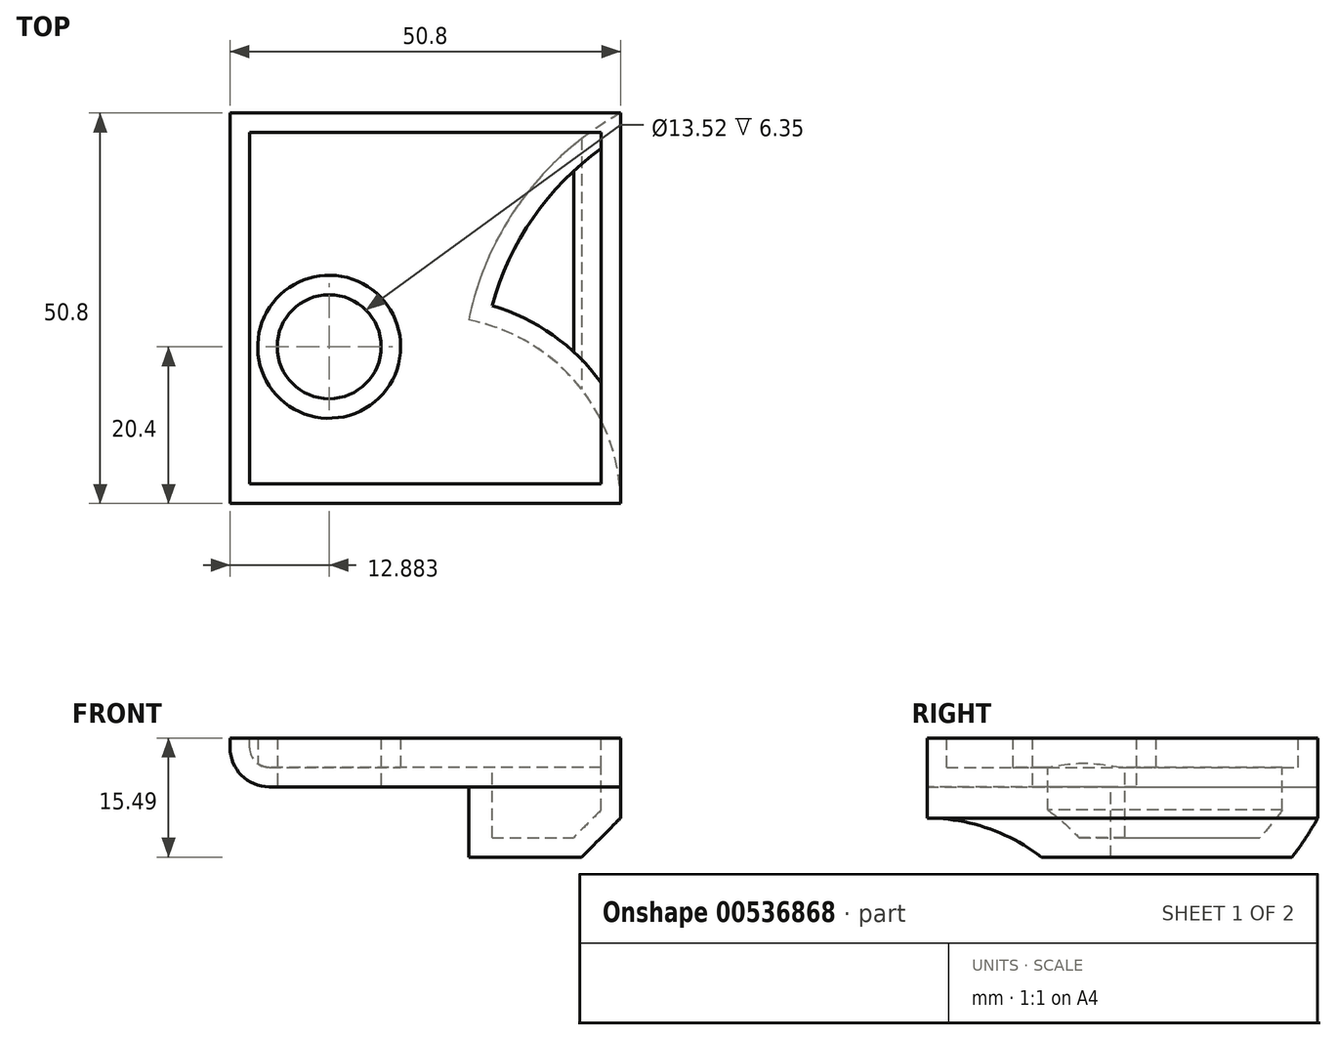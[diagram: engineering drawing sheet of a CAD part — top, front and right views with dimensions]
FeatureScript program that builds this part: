
annotation { "Feature Type Name" : "Feature", "Feature Type Description" : "" }
export const myFeature = defineFeature(function(context is Context, id is Id, definition is map)
    precondition{}
    {
        {
            var Q0;
            Q0=qCreatedBy(makeId("Top.planeOp"),FACE);
            var sketch = newSketch(context, id + "F0", { "sketchPlane" : qUnion([Q0])});
            skLineSegment(sketch, "E0.bottom", {"start": v(0, 0) * mm, "end": v(-50.8, 0) * mm});
            skLineSegment(sketch, "E0.top", {"start": v(0, 50.8) * mm, "end": v(-50.8, 50.8) * mm});
            skLineSegment(sketch, "E0.left", {"start": v(0, 0) * mm, "end": v(0, 50.8) * mm});
            skLineSegment(sketch, "E0.right", {"start": v(-50.8, 0) * mm, "end": v(-50.8, 50.8) * mm});
            skSolve(sketch);
        }
        {
            var Q0;
            Q0=makeQuery(id+"F0.imprint","IMPRINT",FACE,{"disambiguationData":[TD([[makeQuery(id+"F0.imprint","IMPRINT",EDGE,{"derivedFrom":sQuery(id+"F0.wireOp",EDGE,"E0.bottom")}),-1.0]])]});
            extrude(context, id + "F1", {"entities" : qUnion([Q0]), "oppositeDirection" : true, "depth" : 6.35 * mm, "offsetDistance" : 25.4 * mm});
        }
        {
            var Q0;
            Q0=makeQuery(id+"F1.opExtrude","CAP_FACE",FACE,{"disambiguationData":[OSD([sQuery(id+"F0.wireOp",EDGE,"E0.bottom"),sQuery(id+"F0.wireOp",EDGE,"E0.top"),sQuery(id+"F0.wireOp",EDGE,"E0.left"),sQuery(id+"F0.wireOp",EDGE,"E0.right")])],"isStart":false});
            var sketch = newSketch(context, id + "F2", { "sketchPlane" : qUnion([Q0])});
            skArc(sketch, "E1", {"start": v(-19.78, -23.88) * mm, "mid": v(-12.85, -39.52) * mm, "end": v(0, -50.8) * mm});
            skArc(sketch, "E2", {"start": v(-19.78, -23.88) * mm, "mid": v(-5.59, -15.5) * mm, "end": v(0, 0) * mm});
            skCircle(sketch, "E3", {"center": v(-37.92, -20.4) * mm, "radius": 6.76 * mm});
            skSolve(sketch);
        }
        {
            var Q0;
            Q0=makeQuery(id+"F2.imprint","IMPRINT",FACE,{"disambiguationData":[TD([[makeQuery(id+"F2.imprint","IMPRINT",EDGE,{"derivedFrom":sQuery(id+"F2.wireOp",EDGE,"E1")}),1.0]])]});
            extrude(context, id + "F3", {"entities" : qUnion([Q0]), "operationType" : NewBodyOperationType.ADD, "depth" : 9.14 * mm, "offsetDistance" : 25.4 * mm});
        }
        {
            var Q0;
            Q0 = qSketchRegion(id + "F2", true);
            extrude(context, id + "F4", {"entities" : qUnion([Q0]), "operationType" : NewBodyOperationType.REMOVE, "oppositeDirection" : true, "depth" : 25.4 * mm, "offsetDistance" : 25.4 * mm});
        }
        {
            var Q0;
            Q0=makeQuery(id+"F1.opExtrude","CAP_EDGE",EDGE,{"disambiguationData":[OSD([sQuery(id+"F0.wireOp",EDGE,"E0.right")])],"isStart":false});
            fillet(context, id + "F5", {"entities" : qUnion([Q0]), "radius" : 5.08 * mm, "tangentPropagation" : true, "allowEdgeOverflow" : false});
        }
        {
            var Q0;
            Q0=makeQuery(id+"F3.opExtrude","CAP_EDGE",EDGE,{"disambiguationData":[OSD([sQuery(id+"F0.wireOp",EDGE,"E0.left")])],"isStart":false});
            chamfer(context, id + "F6", {"entities" : qUnion([Q0]), "width" : 5.08 * mm, "tangentPropagation" : true});
        }
        {
            var Q0;
            Q0=makeQuery(id+"F1.opExtrude","CAP_FACE",FACE,{"disambiguationData":[OSD([sQuery(id+"F0.wireOp",EDGE,"E0.bottom"),sQuery(id+"F0.wireOp",EDGE,"E0.top"),sQuery(id+"F0.wireOp",EDGE,"E0.left"),sQuery(id+"F0.wireOp",EDGE,"E0.right")])],"isStart":true});
            shell(context, id + "F7", {"entities" : qUnion([Q0]), "thickness" : 2.54 * mm});
        }
    });
